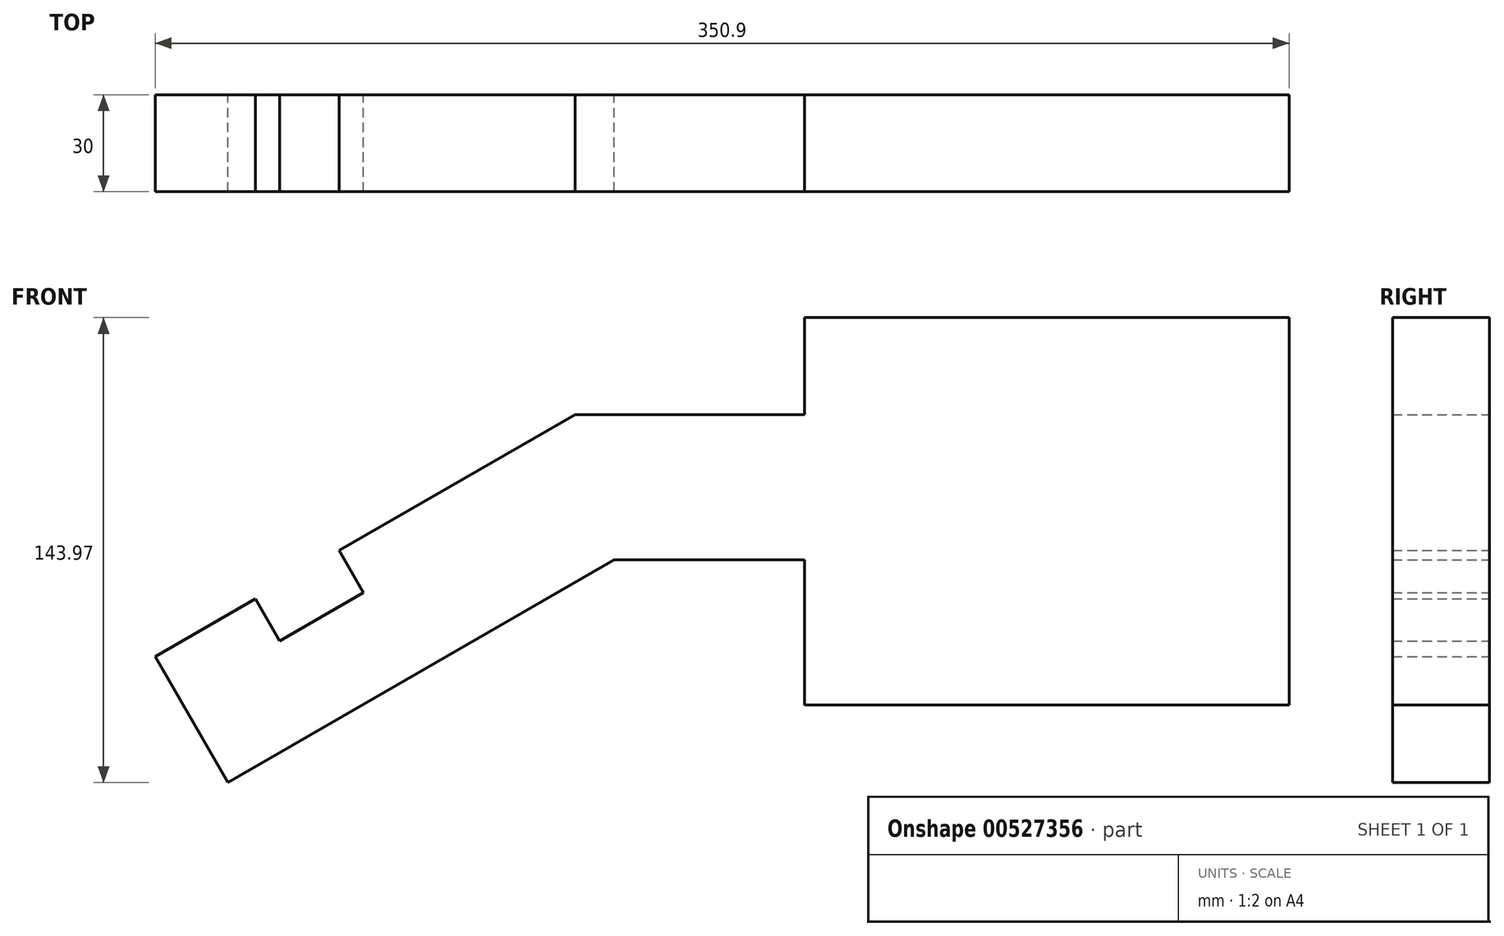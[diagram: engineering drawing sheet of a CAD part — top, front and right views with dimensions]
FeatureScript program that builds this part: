
annotation { "Feature Type Name" : "Feature", "Feature Type Description" : "" }
export const myFeature = defineFeature(function(context is Context, id is Id, definition is map)
    precondition{}
    {
        {
            var Q0;
            Q0=qCreatedBy(makeId("Front.planeOp"),FACE);
            var sketch = newSketch(context, id + "F0", { "sketchPlane" : qUnion([Q0])});
            skLineSegment(sketch, "E0", {"start": v(-118.83, 113.97) * mm, "end": v(1.17, 113.97) * mm});
            skLineSegment(sketch, "E1", {"start": v(1.17, 113.97) * mm, "end": v(1.17, 68.97) * mm});
            skLineSegment(sketch, "E2", {"start": v(1.17, 68.97) * mm, "end": v(-106.77, 68.97) * mm});
            skLineSegment(sketch, "E3", {"start": v(-106.77, 68.97) * mm, "end": v(-226.23, 0) * mm});
            skLineSegment(sketch, "E4", {"start": v(-226.23, 0) * mm, "end": v(-248.73, 38.97) * mm});
            skLineSegment(sketch, "E5", {"start": v(-248.73, 38.97) * mm, "end": v(-217.76, 56.85) * mm});
            skLineSegment(sketch, "E6", {"start": v(-217.76, 56.85) * mm, "end": v(-210.26, 43.86) * mm});
            skLineSegment(sketch, "E7", {"start": v(-210.26, 43.86) * mm, "end": v(-184.28, 58.86) * mm});
            skLineSegment(sketch, "E8", {"start": v(-184.28, 58.86) * mm, "end": v(-191.78, 71.85) * mm});
            skLineSegment(sketch, "E9", {"start": v(-191.78, 71.85) * mm, "end": v(-118.83, 113.97) * mm});
            skLineSegment(sketch, "E10", {"start": v(-47.83, 68.97) * mm, "end": v(-47.83, 23.97) * mm});
            skLineSegment(sketch, "E11", {"start": v(-47.83, 23.97) * mm, "end": v(102.17, 23.97) * mm});
            skLineSegment(sketch, "E12", {"start": v(102.17, 23.97) * mm, "end": v(102.17, 143.97) * mm});
            skLineSegment(sketch, "E13", {"start": v(102.17, 143.97) * mm, "end": v(-47.83, 143.97) * mm});
            skLineSegment(sketch, "E14", {"start": v(-47.83, 143.97) * mm, "end": v(-47.83, 113.97) * mm});
            skSolve(sketch);
        }
        {
            var Q0;
            {var subQ6=sQuery(id+"F0.wireOp",EDGE,"E1");Q0=makeQuery(id+"F0.imprint","IMPRINT",FACE,{"disambiguationData":[TD([[makeQuery(id+"F0.imprint","IMPRINT",EDGE,{"derivedFrom":subQ6}),-1.0]])]});}
            var Q1;
            {var subQ1=sQuery(id+"F0.wireOp",EDGE,"E1");Q1=makeQuery(id+"F0.imprint","IMPRINT",FACE,{"disambiguationData":[TD([[makeQuery(id+"F0.imprint","IMPRINT",EDGE,{"derivedFrom":subQ1}),1.0]])]});}
            extrude(context, id + "F1", {"entities" : qUnion([Q0, Q1]), "depth" : 30 * mm, "offsetDistance" : 25 * mm});
        }
    });
